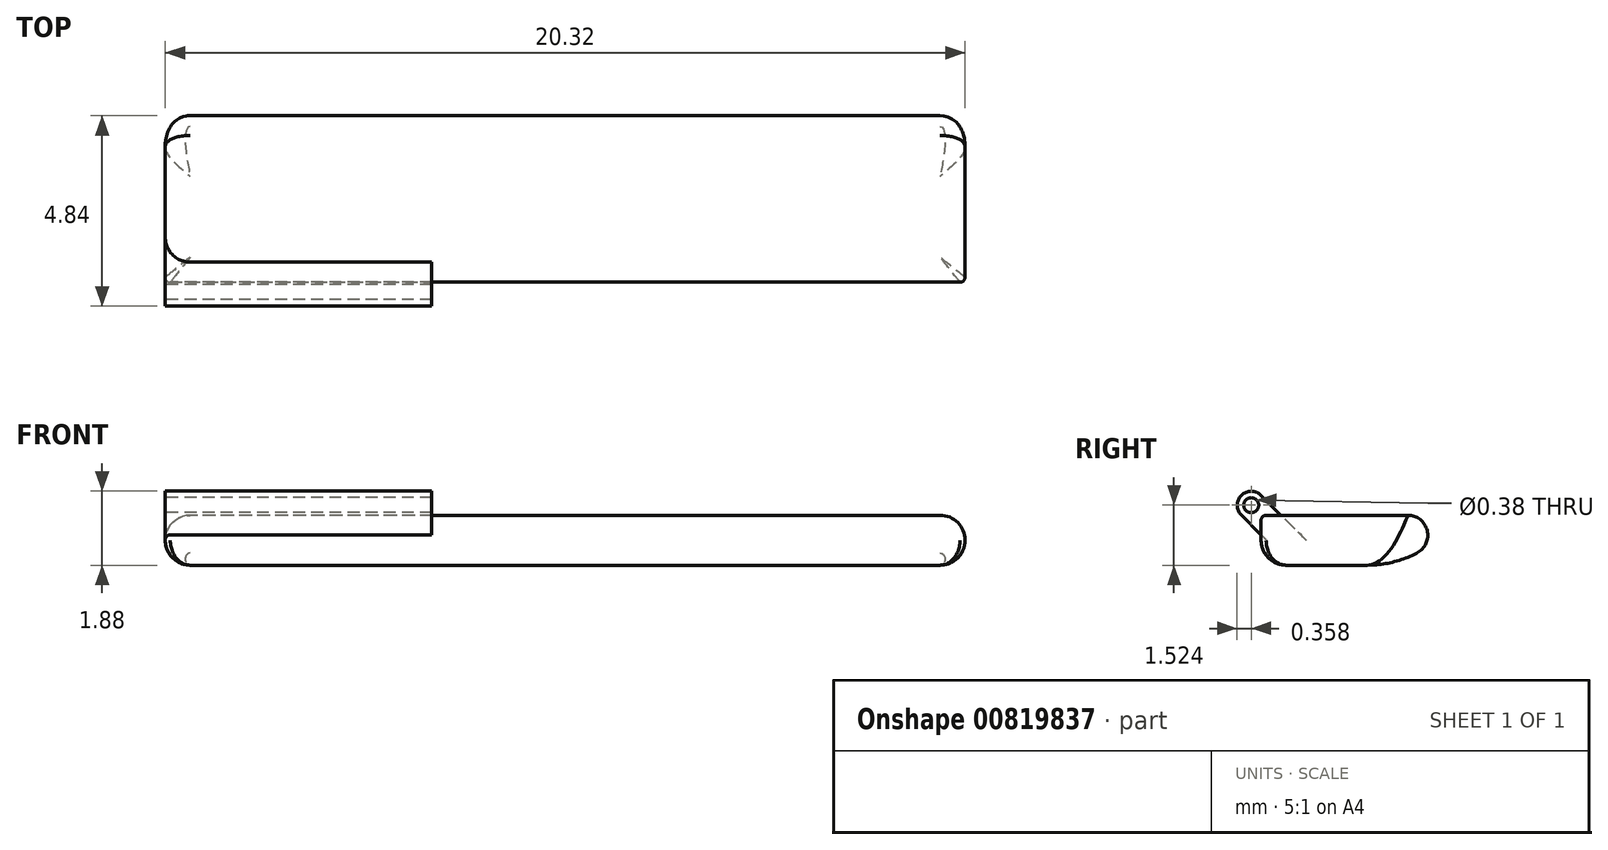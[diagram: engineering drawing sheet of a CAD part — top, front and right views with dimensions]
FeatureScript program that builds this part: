
annotation { "Feature Type Name" : "Feature", "Feature Type Description" : "" }
export const myFeature = defineFeature(function(context is Context, id is Id, definition is map)
    precondition{}
    {
        {
            var Q0;
            Q0=qCreatedBy(makeId("Top.planeOp"),FACE);
            var sketch = newSketch(context, id + "F0", { "sketchPlane" : qUnion([Q0])});
            skLineSegment(sketch, "E0.bottom", {"start": v(0, 0) * mm, "end": v(20.32, 0) * mm});
            skLineSegment(sketch, "E0.top", {"start": v(0, 8.46) * mm, "end": v(20.32, 8.46) * mm});
            skLineSegment(sketch, "E0.left", {"start": v(0, 0) * mm, "end": v(0, 8.46) * mm});
            skLineSegment(sketch, "E0.right", {"start": v(20.32, 0) * mm, "end": v(20.32, 8.46) * mm});
            skSolve(sketch);
        }
        {
            var Q0;
            Q0=qSketchRegion(id+"F0",true);
            extrude(context, id + "F1", {"entities" : qUnion([Q0]), "depth" : 1.27 * mm, "offsetDistance" : 25.4 * mm});
        }
        {
            var Q0;
            Q0=qCreatedBy(makeId("Right.planeOp"),FACE);
            var sketch = newSketch(context, id + "F2", { "sketchPlane" : qUnion([Q0])});
            skLineSegment(sketch, "E1", {"start": v(0, 1.27) * mm, "end": v(-0.25, 1.52) * mm});
            skCircle(sketch, "E2", {"center": v(-0.25, 1.52) * mm, "radius": 0.36 * mm});
            skLineSegment(sketch, "E3.0", {"start": v(0, 1.27) * mm, "end": v(8.46, 1.27) * mm});
            skLineSegment(sketch, "E4.0", {"start": v(0, 1.27) * mm, "end": v(0, 0) * mm});
            skLineSegment(sketch, "E5", {"start": v(-0.25, 1.52) * mm, "end": v(-0.5, 1.27) * mm});
            skLineSegment(sketch, "E6", {"start": v(-0.25, 1.52) * mm, "end": v(0, 1.78) * mm});
            skLineSegment(sketch, "E7", {"start": v(0, 1.78) * mm, "end": v(0.5, 1.27) * mm});
            skLineSegment(sketch, "E8", {"start": v(-0.5, 1.27) * mm, "end": v(0, 0.77) * mm});
            skSolve(sketch);
        }
        {
            var Q0;
            Q0=qSketchRegion(id+"F2",true);
            extrude(context, id + "F3", {"entities" : qUnion([Q0]), "operationType" : NewBodyOperationType.ADD, "depth" : 6.77 * mm, "offsetDistance" : 25.4 * mm});
        }
        {
            var Q0;
            Q0=makeQuery(id+"F3.boolean.opBoolean","MERGE",FACE,{"derivedFrom":[makeQuery(id+"F1.opExtrude","SWEPT_FACE",FACE,{"disambiguationData":[OSD([sQuery(id+"F0.wireOp",EDGE,"E0.left")])]}),makeQuery(id+"F3.opExtrude","CAP_FACE",FACE,{"disambiguationData":[OSD([sQuery(id+"F2.wireOp",EDGE,"E2"),sQuery(id+"F2.wireOp",EDGE,"E3.0"),sQuery(id+"F2.wireOp",EDGE,"E4.0"),sQuery(id+"F2.wireOp",EDGE,"E7"),sQuery(id+"F2.wireOp",EDGE,"E8")])],"isStart":true})]});
            cPlane(context, id + "F4", {"entities" : qUnion([Q0]), "cplaneType" : CPlaneType.OFFSET, "offset" : 10.16 * mm, "oppositeDirection" : true, "width" : 152.4 * mm, "height" : 152.4 * mm});
        }
        {
            var Q0;
            Q0=qCreatedBy(id+"F4.planeOp",FACE);
            var sketch = newSketch(context, id + "F5", { "sketchPlane" : qUnion([Q0])});
            skLineSegment(sketch, "E9.0", {"start": v(-0.5, 1.27) * mm, "end": v(-8.46, 1.27) * mm});
            skLineSegment(sketch, "E10.0", {"start": v(-8.46, 1.27) * mm, "end": v(-8.46, 0) * mm});
            skLineSegment(sketch, "E11", {"start": v(-8.46, 1.27) * mm, "end": v(-8.7, 1.52) * mm});
            skCircle(sketch, "E12", {"center": v(-8.7, 1.52) * mm, "radius": 0.36 * mm});
            skLineSegment(sketch, "E13", {"start": v(-8.7, 1.52) * mm, "end": v(-8.46, 1.77) * mm});
            skLineSegment(sketch, "E14", {"start": v(-8.46, 1.77) * mm, "end": v(-7.96, 1.27) * mm});
            skLineSegment(sketch, "E15", {"start": v(-8.7, 1.52) * mm, "end": v(-8.96, 1.27) * mm});
            skLineSegment(sketch, "E16", {"start": v(-8.96, 1.27) * mm, "end": v(-8.46, 0.77) * mm});
            skSolve(sketch);
        }
        {
            var Q0;
            Q0=qSketchRegion(id+"F5",true);
            extrude(context, id + "F6", {"entities" : qUnion([Q0]), "operationType" : NewBodyOperationType.ADD, "depth" : 3.4 * mm, "offsetDistance" : 25.4 * mm, "hasSecondDirection" : true, "secondDirectionOppositeDirection" : true, "secondDirectionDepth" : 3.4 * mm});
        }
        {
            var Q0;
            Q0=makeQuery(id+"F6.opExtrude","CAP_FACE",FACE,{"disambiguationData":[OSD([sQuery(id+"F5.wireOp",EDGE,"E9.0"),sQuery(id+"F5.wireOp",EDGE,"E10.0"),sQuery(id+"F5.wireOp",EDGE,"E12"),sQuery(id+"F5.wireOp",EDGE,"E14"),sQuery(id+"F5.wireOp",EDGE,"E16")])],"isStart":false});
            var sketch = newSketch(context, id + "F7", { "sketchPlane" : qUnion([Q0])});
            skCircle(sketch, "E17", {"center": v(-8.7, 1.52) * mm, "radius": 0.2 * mm});
            skArc(sketch, "E18.0", {"start": v(0, 1.78) * mm, "mid": v(0.5, 1.78) * mm, "end": v(0.5, 1.27) * mm});
            skCircle(sketch, "E19", {"center": v(0.25, 1.52) * mm, "radius": 0.2 * mm});
            skSolve(sketch);
        }
        {
            var Q0;
            Q0=qSketchRegion(id+"F7",true);
            extrude(context, id + "F8", {"entities" : qUnion([Q0]), "operationType" : NewBodyOperationType.REMOVE, "oppositeDirection" : true, "depth" : 25.4 * mm, "offsetDistance" : 25.4 * mm, "hasSecondDirection" : true, "secondDirectionOppositeDirection" : false, "secondDirectionDepth" : 25.4 * mm});
        }
        {
            var Q0;
            Q0=makeQuery(id+"F1.opExtrude","CAP_EDGE",EDGE,{"disambiguationData":[OSD([sQuery(id+"F0.wireOp",EDGE,"E0.bottom")])],"isStart":true});
            var Q1;
            Q1=makeQuery(id+"F1.opExtrude","CAP_EDGE",EDGE,{"disambiguationData":[OSD([sQuery(id+"F0.wireOp",EDGE,"E0.top")])],"isStart":true});
            var Q2;
            {var subQ0=sQuery(id+"F0.wireOp",EDGE,"E0.left");var subQ1=sQuery(id+"F0.wireOp",EDGE,"E0.top");Q2=makeQuery(id+"F6.boolean.opBoolean","SPLIT",EDGE,{"disambiguationData":[TD([makeQuery(id+"F1.opExtrude","SWEPT_FACE",FACE,{"disambiguationData":[OSD([subQ0])]})])],"derivedFrom":makeQuery(id+"F1.opExtrude","CAP_EDGE",EDGE,{"disambiguationData":[OSD([subQ1])],"isStart":false})});}
            var Q3;
            Q3=makeQuery(id+"F1.opExtrude","CAP_EDGE",EDGE,{"disambiguationData":[OSD([sQuery(id+"F0.wireOp",EDGE,"E0.left")])],"isStart":false});
            var Q4;
            Q4=makeQuery(id+"F1.opExtrude","CAP_EDGE",EDGE,{"disambiguationData":[OSD([sQuery(id+"F0.wireOp",EDGE,"E0.left")])],"isStart":true});
            var Q5;
            Q5=makeQuery(id+"F1.opExtrude","CAP_EDGE",EDGE,{"disambiguationData":[OSD([sQuery(id+"F0.wireOp",EDGE,"E0.right")])],"isStart":false});
            var Q6;
            Q6=makeQuery(id+"F1.opExtrude","CAP_EDGE",EDGE,{"disambiguationData":[OSD([sQuery(id+"F0.wireOp",EDGE,"E0.right")])],"isStart":true});
            fillet(context, id + "F9", {"entities" : qUnion([Q0, Q1, Q2, Q3, Q4, Q5, Q6]), "radius" : 0.64 * mm, "tangentPropagation" : true, "allowEdgeOverflow" : false});
        }
        {
            var Q0;
            Q0=makeQuery(id+"F9.opFillet","BLEND_EDGE",EDGE,{"blendedFrom":[makeQuery(id+"F1.opExtrude","CAP_EDGE",EDGE,{"disambiguationData":[OSD([sQuery(id+"F0.wireOp",EDGE,"E0.bottom")])],"isStart":true}),makeQuery(id+"F1.opExtrude","CAP_EDGE",EDGE,{"disambiguationData":[OSD([sQuery(id+"F0.wireOp",EDGE,"E0.left")])],"isStart":true})],"blendedInto":[]});
            var Q1;
            Q1=makeQuery(id+"F9.opFillet","BLEND_EDGE",EDGE,{"blendedFrom":[makeQuery(id+"F1.opExtrude","CAP_EDGE",EDGE,{"disambiguationData":[OSD([sQuery(id+"F0.wireOp",EDGE,"E0.bottom")])],"isStart":true}),makeQuery(id+"F1.opExtrude","CAP_EDGE",EDGE,{"disambiguationData":[OSD([sQuery(id+"F0.wireOp",EDGE,"E0.right")])],"isStart":true})],"blendedInto":[]});
            var Q2;
            Q2=makeQuery(id+"F9.opFillet","BLEND_EDGE",EDGE,{"blendedFrom":[makeQuery(id+"F1.opExtrude","CAP_EDGE",EDGE,{"disambiguationData":[OSD([sQuery(id+"F0.wireOp",EDGE,"E0.top")])],"isStart":true}),makeQuery(id+"F1.opExtrude","CAP_EDGE",EDGE,{"disambiguationData":[OSD([sQuery(id+"F0.wireOp",EDGE,"E0.right")])],"isStart":true})],"blendedInto":[]});
            var Q3;
            Q3=makeQuery(id+"F9.opFillet","BLEND_EDGE",EDGE,{"blendedFrom":[makeQuery(id+"F1.opExtrude","CAP_EDGE",EDGE,{"disambiguationData":[OSD([sQuery(id+"F0.wireOp",EDGE,"E0.top")])],"isStart":true}),makeQuery(id+"F1.opExtrude","CAP_EDGE",EDGE,{"disambiguationData":[OSD([sQuery(id+"F0.wireOp",EDGE,"E0.left")])],"isStart":true})],"blendedInto":[]});
            fillet(context, id + "F10", {"entities" : qUnion([Q0, Q1, Q2, Q3]), "radius" : 0.13 * mm, "tangentPropagation" : true, "allowEdgeOverflow" : false});
        }
        {
            var Q0;
            Q0=qCreatedBy(makeId("Right.planeOp"),FACE);
            var sketch = newSketch(context, id + "F11", { "sketchPlane" : qUnion([Q0])});
            skLineSegment(sketch, "E20.bottom", {"start": v(5.04, 3.43) * mm, "end": v(10.3, 3.43) * mm});
            skLineSegment(sketch, "E20.top", {"start": v(5.04, -1.53) * mm, "end": v(10.3, -1.53) * mm});
            skLineSegment(sketch, "E20.left", {"start": v(5.04, 3.43) * mm, "end": v(5.04, -1.53) * mm});
            skLineSegment(sketch, "E20.right", {"start": v(10.3, 3.43) * mm, "end": v(10.3, -1.53) * mm});
            skSolve(sketch);
        }
        {
            var Q0;
            Q0 = qSketchRegion(id + "F11", true);
            extrude(context, id + "F12", {"entities" : qUnion([Q0]), "operationType" : NewBodyOperationType.REMOVE, "oppositeDirection" : true, "depth" : 25.4 * mm, "offsetDistance" : 25.4 * mm, "hasSecondDirection" : true, "secondDirectionOppositeDirection" : false, "secondDirectionDepth" : 25.4 * mm});
        }
        {
            var Q0;
            Q0=qCreatedBy(id+"F4.planeOp",FACE);
            var sketch = newSketch(context, id + "F13", { "sketchPlane" : qUnion([Q0])});
            skArc(sketch, "E21", {"start": v(-5.11, 1.45) * mm, "mid": v(-4.1, 0.39) * mm, "end": v(-2.69, 0) * mm});
            skLineSegment(sketch, "E22", {"start": v(-5.11, 1.45) * mm, "end": v(-5.11, -0.47) * mm});
            skLineSegment(sketch, "E23", {"start": v(-5.11, -0.47) * mm, "end": v(-2.69, 0) * mm});
            skSolve(sketch);
        }
        {
            var Q0;
            Q0 = qSketchRegion(id + "F13", true);
            extrude(context, id + "F14", {"entities" : qUnion([Q0]), "operationType" : NewBodyOperationType.REMOVE, "oppositeDirection" : true, "depth" : 25.4 * mm, "offsetDistance" : 25.4 * mm, "hasSecondDirection" : true, "secondDirectionOppositeDirection" : false, "secondDirectionDepth" : 25.4 * mm});
        }
        {
            var Q0;
            Q0=makeQuery(id+"F14.boolean.opBoolean","INTERSECT",EDGE,{"derivedFrom":[makeQuery(id+"F9.opFillet","BLEND_FACE",FACE,{"disambiguationData":[OSD([sQuery(id+"F0.wireOp",EDGE,"E0.right")])]}),makeQuery(id+"F14.opExtrude","SWEPT_FACE",FACE,{"disambiguationData":[OSD([sQuery(id+"F13.wireOp",EDGE,"E21")])]})]});
            fillet(context, id + "F15", {"entities" : qUnion([Q0]), "radius" : 0.5 * mm, "tangentPropagation" : true, "allowEdgeOverflow" : false});
        }
    });
